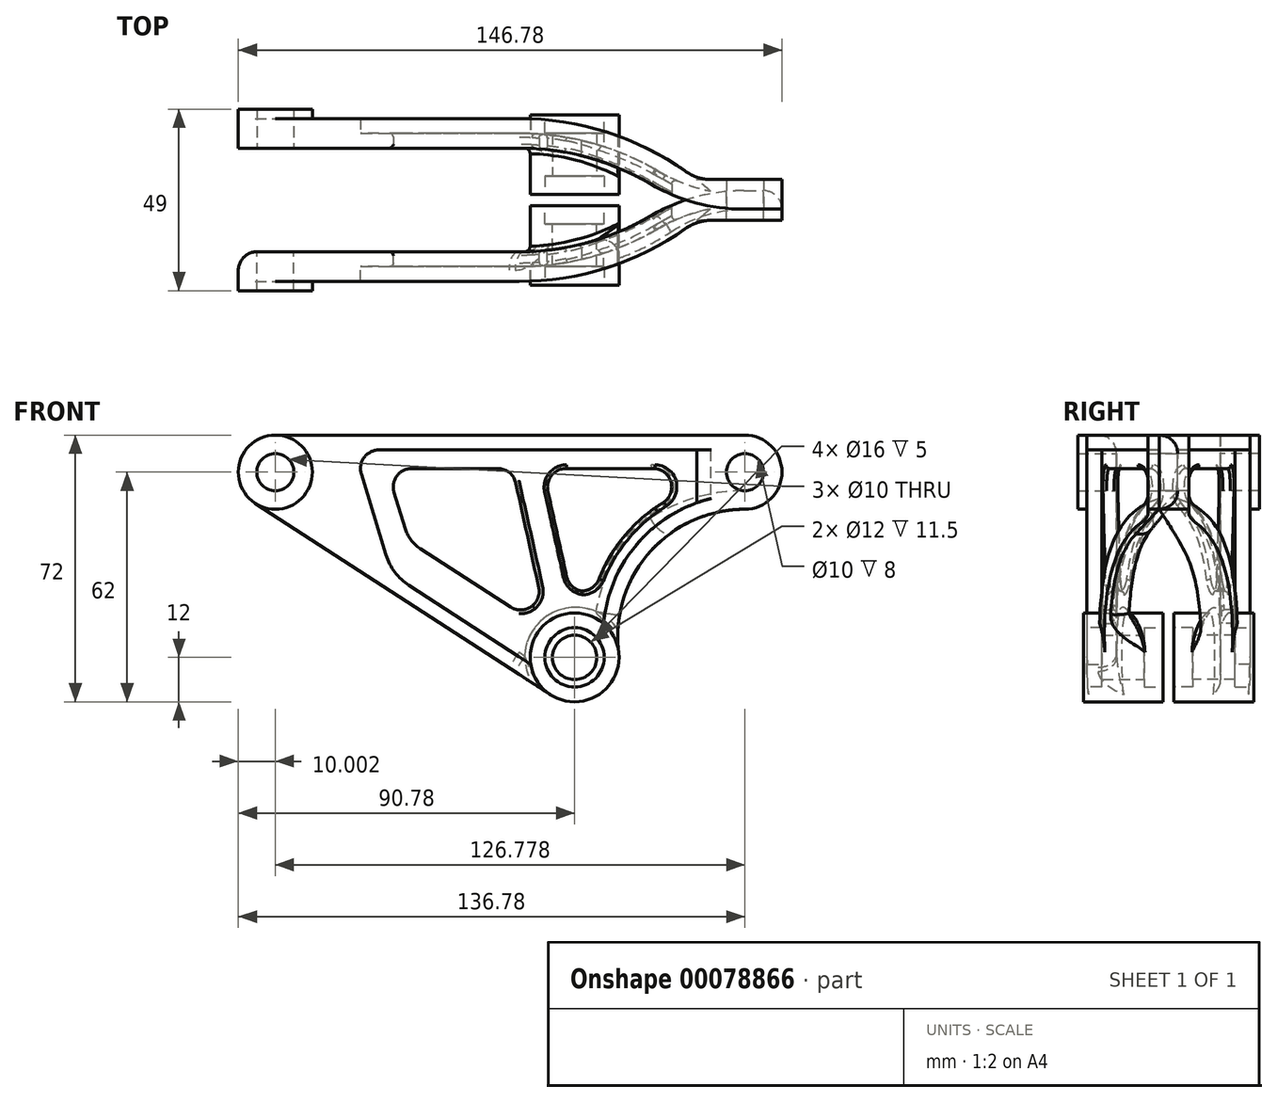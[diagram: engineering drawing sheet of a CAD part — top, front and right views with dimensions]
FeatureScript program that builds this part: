
annotation { "Feature Type Name" : "Feature", "Feature Type Description" : "" }
export const myFeature = defineFeature(function(context is Context, id is Id, definition is map)
    precondition{}
    {
        {
            var Q0;
            Q0=qCreatedBy(makeId("Front.planeOp"),FACE);
            var sketch = newSketch(context, id + "F0", { "sketchPlane" : qUnion([Q0])});
            skCircle(sketch, "E0", {"center": v(0, 0) * mm, "radius": 6 * mm});
            skCircle(sketch, "E1", {"center": v(0, 0) * mm, "radius": 12 * mm});
            skLineSegment(sketch, "E2", {"start": v(0, 0) * mm, "end": v(0, 50) * mm, "construction": true});
            skLineSegment(sketch, "E3", {"start": v(0, 50) * mm, "end": v(-80.78, 50) * mm, "construction": true});
            skLineSegment(sketch, "E4", {"start": v(-80.78, 50) * mm, "end": v(0, 0) * mm, "construction": true});
            skLineSegment(sketch, "E5", {"start": v(0, 0) * mm, "end": v(46, 50) * mm, "construction": true});
            skLineSegment(sketch, "E6", {"start": v(46, 50) * mm, "end": v(0, 50) * mm, "construction": true});
            skCircle(sketch, "E7", {"center": v(-80.78, 50) * mm, "radius": 10 * mm});
            skCircle(sketch, "E8", {"center": v(46, 50) * mm, "radius": 10 * mm});
            skCircle(sketch, "E9", {"center": v(46, 50) * mm, "radius": 6 * mm});
            skCircle(sketch, "E10", {"center": v(-80.78, 50) * mm, "radius": 6 * mm});
            skLineSegment(sketch, "E11", {"start": v(-80.78, 60) * mm, "end": v(46, 60) * mm});
            skLineSegment(sketch, "E12", {"start": v(-86.22, 41.6) * mm, "end": v(-6.53, -10.07) * mm});
            skLineSegment(sketch, "E13", {"start": v(53.56, 43.45) * mm, "end": v(9.07, -7.86) * mm, "construction": true});
            skArc(sketch, "E14", {"start": v(46, 40) * mm, "mid": v(20.27, 28.41) * mm, "end": v(11.91, 1.46) * mm});
            skSolve(sketch);
        }
        {
            var Q0;
            {var subQ0=makeQuery(id+"F0.imprint","IMPRINT",EDGE,{"derivedFrom":sQuery(id+"F0.wireOp",EDGE,"E0")});var subQ1=makeQuery(id+"F0.imprint","IMPRINT",EDGE,{"derivedFrom":sQuery(id+"F0.wireOp",EDGE,"E9")});var subQ2=makeQuery(id+"F0.imprint","IMPRINT",EDGE,{"derivedFrom":sQuery(id+"F0.wireOp",EDGE,"E10")});var subQ11=sQuery(id+"F0.wireOp",EDGE,"E11");Q0=qUnion([makeQuery(id+"F0.imprint","IMPRINT",FACE,{"disambiguationData":[TD([[subQ0,1.0]])]}),makeQuery(id+"F0.imprint","IMPRINT",FACE,{"disambiguationData":[TD([[subQ1,1.0]])]}),makeQuery(id+"F0.imprint","IMPRINT",FACE,{"disambiguationData":[TD([[subQ2,1.0]])]}),makeQuery(id+"F0.imprint","IMPRINT",FACE,{"disambiguationData":[TD([[subQ0,-1.0]])]}),makeQuery(id+"F0.imprint","IMPRINT",FACE,{"disambiguationData":[TD([[subQ2,-1.0]])]}),makeQuery(id+"F0.imprint","IMPRINT",FACE,{"disambiguationData":[TD([[subQ1,-1.0]])]}),makeQuery(id+"F0.imprint","IMPRINT",FACE,{"disambiguationData":[TD([[makeQuery(id+"F0.imprint","IMPRINT",EDGE,{"derivedFrom":subQ11}),-1.0]])]})]);}
            extrude(context, id + "F1", {"entities" : qUnion([Q0]), "depth" : 22 * mm});
        }
        {
            var Q0;
            Q0=makeQuery(id+"F1.opExtrude","CAP_FACE",FACE,{"disambiguationData":[OSD([sQuery(id+"F0.wireOp",EDGE,"E1"),sQuery(id+"F0.wireOp",EDGE,"E7"),sQuery(id+"F0.wireOp",EDGE,"E8"),sQuery(id+"F0.wireOp",EDGE,"E11"),sQuery(id+"F0.wireOp",EDGE,"E12"),sQuery(id+"F0.wireOp",EDGE,"E14")])],"isStart":true});
            extrude(context, id + "F2", {"entities" : qUnion([Q0]), "operationType" : NewBodyOperationType.ADD, "depth" : 2.5 * mm});
        }
        {
            var Q0;
            {var subQ0=sQuery(id+"F0.wireOp",EDGE,"E11");Q0=makeQuery(id+"F2.boolean.opBoolean","MERGE",FACE,{"derivedFrom":[makeQuery(id+"F1.opExtrude","SWEPT_FACE",FACE,{"disambiguationData":[OSD([subQ0])]}),makeQuery(id+"F2.opExtrude","SWEPT_FACE",FACE,{"disambiguationData":[OSD([subQ0])]})]});}
            var sketch = newSketch(context, id + "F3", { "sketchPlane" : qUnion([Q0])});
            skLineSegment(sketch, "E15", {"start": v(-100, -14) * mm, "end": v(-15, -14) * mm});
            skArc(sketch, "E16", {"start": v(-15, -14) * mm, "mid": v(15.45, -7.03) * mm, "end": v(39.84, 12.5) * mm});
            skLineSegment(sketch, "E17", {"start": v(-100, -14) * mm, "end": v(-100, 12.5) * mm});
            skLineSegment(sketch, "E18", {"start": v(-100, 12.5) * mm, "end": v(39.84, 12.5) * mm});
            skArc(sketch, "E19.0", {"start": v(-15, -22) * mm, "mid": v(10.37, -17.76) * mm, "end": v(32.98, -5.5) * mm});
            skLineSegment(sketch, "E20", {"start": v(-15, -22) * mm, "end": v(-15, -32) * mm});
            skLineSegment(sketch, "E21", {"start": v(-15, -32) * mm, "end": v(70, -32) * mm});
            skLineSegment(sketch, "E22", {"start": v(70, -32) * mm, "end": v(70, -5.5) * mm});
            skLineSegment(sketch, "E23", {"start": v(70, -5.5) * mm, "end": v(32.98, -5.5) * mm});
            skSolve(sketch);
        }
        {
            var Q0;
            {var subQ3=sQuery(id+"F3.wireOp",EDGE,"E15");var subQ8=sQuery(id+"F3.wireOp",EDGE,"E16");var subQ12=sQuery(id+"F3.wireOp",EDGE,"E17");var subQ20=sQuery(id+"F3.wireOp",EDGE,"E19.0");var subQ21=sQuery(id+"F3.wireOp",EDGE,"E20");var subQ24=makeQuery(id+"F3.imprint","INTERSECT",VERTEX,{"derivedFrom":[subQ3,subQ8]});Q0=qUnion([makeQuery(id+"F3.imprint","IMPRINT",FACE,{"disambiguationData":[TD([[makeQuery(id+"F3.imprint","IMPRINT",EDGE,{"derivedFrom":subQ12}),-1.0]])]}),makeQuery(id+"F3.imprint","IMPRINT",FACE,{"disambiguationData":[TD([[makeQuery(id+"F3.imprint","IMPRINT",EDGE,{"derivedFrom":subQ21}),1.0]])]}),makeQuery(id+"F3.imprint","IMPRINT",FACE,{"disambiguationData":[TD([[makeQuery(id+"F3.imprint","IMPRINT",EDGE,{"disambiguationData":[TD([[subQ24,-1.0]])],"derivedFrom":subQ8}),1.0]])]}),makeQuery(id+"F3.imprint","IMPRINT",FACE,{"disambiguationData":[TD([[makeQuery(id+"F3.imprint","IMPRINT",EDGE,{"derivedFrom":subQ20}),-1.0]])]})]);}
            extrude(context, id + "F4", {"entities" : qUnion([Q0]), "operationType" : NewBodyOperationType.REMOVE, "endBound" : BoundingType.THROUGH_ALL, "oppositeDirection" : true, "depth" : 25 * mm});
        }
        {
            var Q0;
            Q0=makeQuery(id+"F4.boolean.opBoolean","INTERSECT",EDGE,{"derivedFrom":[makeQuery(id+"F2.opExtrude","CAP_FACE",FACE,{"disambiguationData":[OSD([sQuery(id+"F0.wireOp",EDGE,"E1"),sQuery(id+"F0.wireOp",EDGE,"E7"),sQuery(id+"F0.wireOp",EDGE,"E8"),sQuery(id+"F0.wireOp",EDGE,"E11"),sQuery(id+"F0.wireOp",EDGE,"E12"),sQuery(id+"F0.wireOp",EDGE,"E14")])],"isStart":false}),makeQuery(id+"F4.opExtrude","SWEPT_FACE",FACE,{"disambiguationData":[OSD([sQuery(id+"F3.wireOp",EDGE,"E16")])]})]});
            var Q1;
            Q1=makeQuery(id+"F4.opExtrude","SWEPT_EDGE",EDGE,{"disambiguationData":[OSD([sQuery(id+"F3.imprint",VERTEX,"E19.0.end")])]});
            fillet(context, id + "F5", {"entities" : qUnion([Q0, Q1]), "radius" : 50 * mm, "tangentPropagation" : true, "allowEdgeOverflow" : false});
        }
        {
            var Q0;
            Q0=makeQuery(id+"F1.opExtrude","CAP_FACE",FACE,{"disambiguationData":[OSD([sQuery(id+"F0.wireOp",EDGE,"E1"),sQuery(id+"F0.wireOp",EDGE,"E7"),sQuery(id+"F0.wireOp",EDGE,"E8"),sQuery(id+"F0.wireOp",EDGE,"E11"),sQuery(id+"F0.wireOp",EDGE,"E12"),sQuery(id+"F0.wireOp",EDGE,"E14")])],"isStart":false});
            var Q1;
            Q1=makeQuery(id+"F4.opExtrude","SWEPT_FACE",FACE,{"disambiguationData":[OSD([sQuery(id+"F3.imprint",EDGE,"E19.0")])]});
            var Q2;
            Q2=makeQuery(id+"F5.opFillet","BLEND_FACE",FACE,{"disambiguationData":[OSD([sQuery(id+"F3.imprint",VERTEX,"E19.0.end")])]});
            var Q3;
            Q3=makeQuery(id+"F4.opExtrude","SWEPT_FACE",FACE,{"disambiguationData":[OSD([makeQuery(id+"F3.imprint","SKETCH_ENTITY",EDGE,{"disambiguationData":[TD([[sQuery(id+"F3.imprint",VERTEX,"E22.end"),-1.0]])],"sketchEntityId":"E23"})])]});
            var Q4;
            Q4=makeQuery(id+"F4.boolean.opBoolean","COPY",FACE,{"derivedFrom":makeQuery(id+"F4.opExtrude","SWEPT_FACE",FACE,{"disambiguationData":[OSD([sQuery(id+"F3.wireOp",EDGE,"E19.0")])]})});
            shell(context, id + "F6", {"entities" : qUnion([Q0, Q1, Q2, Q3, Q4]), "thickness" : 4 * mm});
        }
        {
            var Q0;
            Q0=makeQuery(id+"F0.imprint","IMPRINT",FACE,{"disambiguationData":[TD([[makeQuery(id+"F0.imprint","IMPRINT",EDGE,{"derivedFrom":sQuery(id+"F0.wireOp",EDGE,"E0")}),-1.0]])]});
            extrude(context, id + "F7", {"entities" : qUnion([Q0]), "operationType" : NewBodyOperationType.ADD, "depth" : 23 * mm});
        }
        {
            var Q0;
            Q0=makeQuery(id+"F1.opExtrude","CAP_FACE",FACE,{"disambiguationData":[OSD([sQuery(id+"F0.wireOp",EDGE,"E1"),sQuery(id+"F0.wireOp",EDGE,"E7"),sQuery(id+"F0.wireOp",EDGE,"E8"),sQuery(id+"F0.wireOp",EDGE,"E11"),sQuery(id+"F0.wireOp",EDGE,"E12"),sQuery(id+"F0.wireOp",EDGE,"E14")])],"isStart":false});
            var sketch = newSketch(context, id + "F8", { "sketchPlane" : qUnion([Q0])});
            skLineSegment(sketch, "E24", {"start": v(-60.78, 60) * mm, "end": v(-47.47, 16.48) * mm});
            skLineSegment(sketch, "E25.0", {"start": v(-80.78, 60) * mm, "end": v(-60.78, 60) * mm});
            skLineSegment(sketch, "E25.1", {"start": v(-86.22, 41.6) * mm, "end": v(-47.47, 16.48) * mm});
            skArc(sketch, "E26.trimmedOffspring", {"start": v(-80.78, 60) * mm, "mid": v(-90.37, 52.84) * mm, "end": v(-86.22, 41.6) * mm});
            skSolve(sketch);
        }
        {
            var Q0;
            {var subQ4=makeQuery(id+"F6.opShell","OFFSET_EDGE",EDGE,{"disambiguationData":[OSD([sQuery(id+"F0.wireOp",EDGE,"E7")])]});var subQ10=makeQuery(id+"F8.imprint","IMPRINT",EDGE,{"derivedFrom":subQ4});var subQ12=sQuery(id+"F8.wireOp",EDGE,"E25.0");Q0=qUnion([makeQuery(id+"F8.imprint","IMPRINT",FACE,{"disambiguationData":[TD([[subQ10,1.0]])]}),makeQuery(id+"F8.imprint","IMPRINT",FACE,{"disambiguationData":[TD([[makeQuery(id+"F8.imprint","IMPRINT",EDGE,{"derivedFrom":subQ12}),-1.0]])]})]);}
            extrude(context, id + "F9", {"entities" : qUnion([Q0]), "operationType" : NewBodyOperationType.ADD, "oppositeDirection" : true, "depth" : 6 * mm});
        }
        {
            var Q0;
            Q0=makeQuery(id+"F9.boolean.opBoolean","INTERSECT",EDGE,{"derivedFrom":[makeQuery(id+"F6.opShell","OFFSET_FACE",FACE,{"disambiguationData":[OSD([sQuery(id+"F0.wireOp",EDGE,"E12")])]}),makeQuery(id+"F9.opExtrude","SWEPT_FACE",FACE,{"disambiguationData":[OSD([sQuery(id+"F8.wireOp",EDGE,"E24")])]})]});
            fillet(context, id + "F10", {"entities" : qUnion([Q0]), "radius" : 15 * mm, "tangentPropagation" : true, "allowEdgeOverflow" : false});
        }
        {
            var Q0;
            Q0=makeQuery(id+"F9.boolean.opBoolean","INTERSECT",EDGE,{"derivedFrom":[makeQuery(id+"F6.opShell","OFFSET_FACE",FACE,{"disambiguationData":[OSD([sQuery(id+"F0.wireOp",EDGE,"E11")])]}),makeQuery(id+"F9.opExtrude","SWEPT_FACE",FACE,{"disambiguationData":[OSD([sQuery(id+"F8.wireOp",EDGE,"E24")])]})]});
            fillet(context, id + "F11", {"entities" : qUnion([Q0]), "radius" : 5 * mm, "tangentPropagation" : true, "allowEdgeOverflow" : false});
        }
        {
            var Q0;
            Q0=makeQuery(id+"F4.boolean.opBoolean","COPY",FACE,{"derivedFrom":makeQuery(id+"F4.opExtrude","SWEPT_FACE",FACE,{"disambiguationData":[OSD([sQuery(id+"F3.wireOp",EDGE,"E23")])]})});
            var sketch = newSketch(context, id + "F12", { "sketchPlane" : qUnion([Q0])});
            skCircle(sketch, "E27", {"center": v(46, 50) * mm, "radius": 10 * mm});
            skSolve(sketch);
        }
        {
            var Q0;
            Q0=makeQuery(id+"F9.boolean.opBoolean","MERGE",FACE,{"derivedFrom":[makeQuery(id+"F1.opExtrude","CAP_FACE",FACE,{"disambiguationData":[OSD([sQuery(id+"F0.wireOp",EDGE,"E1"),sQuery(id+"F0.wireOp",EDGE,"E7"),sQuery(id+"F0.wireOp",EDGE,"E8"),sQuery(id+"F0.wireOp",EDGE,"E11"),sQuery(id+"F0.wireOp",EDGE,"E12"),sQuery(id+"F0.wireOp",EDGE,"E14")])],"isStart":false}),makeQuery(id+"F9.opExtrude","CAP_FACE",FACE,{"disambiguationData":[OSD([sQuery(id+"F8.wireOp",EDGE,"E24"),sQuery(id+"F8.wireOp",EDGE,"E25.0"),sQuery(id+"F8.wireOp",EDGE,"E25.1"),sQuery(id+"F8.wireOp",EDGE,"E26.trimmedOffspring")])],"isStart":true})]});
            var sketch = newSketch(context, id + "F13", { "sketchPlane" : qUnion([Q0])});
            skCircle(sketch, "E28", {"center": v(-80.78, 50) * mm, "radius": 10 * mm});
            skSolve(sketch);
        }
        {
            var Q0;
            {var subQ0=sQuery(id+"F13.wireOp",EDGE,"E28");var subQ2=makeQuery(id+"F13.imprint","INTERSECT",VERTEX,{"derivedFrom":[makeQuery(id+"F1.opExtrude","CAP_EDGE",EDGE,{"disambiguationData":[OSD([sQuery(id+"F0.wireOp",EDGE,"E11")])],"isStart":false}),subQ0]});Q0=makeQuery(id+"F13.imprint","IMPRINT",FACE,{"disambiguationData":[TD([[makeQuery(id+"F13.imprint","IMPRINT",EDGE,{"disambiguationData":[TD([[subQ2,-1.0]])],"derivedFrom":subQ0}),1.0]])]});}
            extrude(context, id + "F14", {"entities" : qUnion([Q0]), "operationType" : NewBodyOperationType.ADD, "depth" : 2.5 * mm});
        }
        {
            var Q0;
            Q0=qCreatedBy(makeId("Front.planeOp"),FACE);
            var sketch = newSketch(context, id + "F15", { "sketchPlane" : qUnion([Q0])});
            skLineSegment(sketch, "E29", {"start": v(-43.95, 51) * mm, "end": v(-16.73, 51) * mm});
            skLineSegment(sketch, "E30", {"start": v(-48.73, 44.54) * mm, "end": v(-45.77, 34.86) * mm});
            skLineSegment(sketch, "E31", {"start": v(-41.65, 29.4) * mm, "end": v(-13.92, 11.41) * mm});
            skLineSegment(sketch, "E32", {"start": v(-16.73, 51) * mm, "end": v(-8.96, 15.61) * mm});
            skPoint(sketch, "E33.visualSharp", {"position": v(-50.7, 51) * mm});
            skArc(sketch, "E33.filletArc", {"start": v(-43.95, 51) * mm, "mid": v(-47.97, 48.97) * mm, "end": v(-48.73, 44.54) * mm});
            skPoint(sketch, "E34.visualSharp", {"position": v(-44.7, 31.38) * mm});
            skArc(sketch, "E34.filletArc", {"start": v(-45.77, 34.86) * mm, "mid": v(-44.2, 31.76) * mm, "end": v(-41.65, 29.4) * mm});
            skArc(sketch, "E35.trimOffspring", {"start": v(-8.96, 15.61) * mm, "mid": v(-11.63, 13.74) * mm, "end": v(-13.92, 11.41) * mm});
            skLineSegment(sketch, "E36", {"start": v(-8.54, 51) * mm, "end": v(21.22, 51) * mm});
            skLineSegment(sketch, "E37", {"start": v(-8.54, 51) * mm, "end": v(-1.28, 17.95) * mm});
            skArc(sketch, "E38", {"start": v(5.26, 17.21) * mm, "mid": v(2.03, 17.89) * mm, "end": v(-1.28, 17.95) * mm});
            skArc(sketch, "E39", {"start": v(23.84, 41.74) * mm, "mid": v(12.25, 31.22) * mm, "end": v(5.26, 17.21) * mm});
            skArc(sketch, "E40", {"start": v(21.22, 51) * mm, "mid": v(26.04, 47.36) * mm, "end": v(23.84, 41.74) * mm});
            skLineSegment(sketch, "E41", {"start": v(0, 0) * mm, "end": v(-19.78, 90.06) * mm, "construction": true});
            skSolve(sketch);
        }
        {
            var Q0;
            {Q0=qUnion([makeQuery(id+"F15.imprint","IMPRINT",FACE,{"disambiguationData":[TD([[makeQuery(id+"F15.imprint","IMPRINT",EDGE,{"derivedFrom":sQuery(id+"F15.wireOp",EDGE,"E29")}),-1.0]])]}),makeQuery(id+"F15.imprint","IMPRINT",FACE,{"disambiguationData":[TD([[makeQuery(id+"F15.imprint","IMPRINT",EDGE,{"derivedFrom":sQuery(id+"F15.wireOp",EDGE,"E36")}),-1.0]])]})]);}
            extrude(context, id + "F16", {"entities" : qUnion([Q0]), "operationType" : NewBodyOperationType.REMOVE, "endBound" : BoundingType.SYMMETRIC, "depth" : 50 * mm});
        }
        {
            var Q0;
            Q0=makeQuery(id+"F6.opShell","OFFSET_EDGE",EDGE,{"disambiguationData":[OSD([sQuery(id+"F3.wireOp",EDGE,"E19.0"),sQuery(id+"F3.wireOp",EDGE,"E23")]),OD(0.0)]});
            var Q1;
            Q1=makeQuery(id+"F4.boolean.opBoolean","COPY",EDGE,{"derivedFrom":makeQuery(id+"F4.opExtrude","SWEPT_EDGE",EDGE,{"disambiguationData":[OSD([sQuery(id+"F3.wireOp",EDGE,"E19.0"),sQuery(id+"F3.wireOp",EDGE,"E23")])]})});
            fillet(context, id + "F17", {"entities" : qUnion([Q0, Q1]), "radius" : 12 * mm, "tangentPropagation" : true, "allowEdgeOverflow" : false});
        }
        {
            var Q0;
            Q0=makeQuery(id+"F16.boolean.opBoolean","COPY",EDGE,{"derivedFrom":makeQuery(id+"F16.opExtrude","SWEPT_EDGE",EDGE,{"disambiguationData":[OSD([sQuery(id+"F15.wireOp",EDGE,"E29"),sQuery(id+"F15.wireOp",EDGE,"E32")])]})});
            var Q1;
            Q1=makeQuery(id+"F16.boolean.opBoolean","COPY",EDGE,{"derivedFrom":makeQuery(id+"F16.opExtrude","SWEPT_EDGE",EDGE,{"disambiguationData":[OSD([sQuery(id+"F15.wireOp",EDGE,"E31"),sQuery(id+"F15.wireOp",EDGE,"E35.trimOffspring")])]})});
            var Q2;
            Q2=makeQuery(id+"F16.boolean.opBoolean","COPY",EDGE,{"derivedFrom":makeQuery(id+"F16.opExtrude","SWEPT_EDGE",EDGE,{"disambiguationData":[OSD([sQuery(id+"F15.wireOp",EDGE,"E38"),sQuery(id+"F15.wireOp",EDGE,"E39")])]})});
            var Q3;
            Q3=makeQuery(id+"F16.boolean.opBoolean","COPY",EDGE,{"derivedFrom":makeQuery(id+"F16.opExtrude","SWEPT_EDGE",EDGE,{"disambiguationData":[OSD([sQuery(id+"F15.wireOp",EDGE,"E37"),sQuery(id+"F15.wireOp",EDGE,"E38")])]})});
            var Q4;
            Q4=makeQuery(id+"F16.boolean.opBoolean","COPY",EDGE,{"derivedFrom":makeQuery(id+"F16.opExtrude","SWEPT_EDGE",EDGE,{"disambiguationData":[OSD([sQuery(id+"F15.wireOp",EDGE,"E32"),sQuery(id+"F15.wireOp",EDGE,"E35.trimOffspring")])]})});
            var Q5;
            Q5=makeQuery(id+"F16.boolean.opBoolean","COPY",EDGE,{"derivedFrom":makeQuery(id+"F16.opExtrude","SWEPT_EDGE",EDGE,{"disambiguationData":[OSD([sQuery(id+"F15.wireOp",EDGE,"E36"),sQuery(id+"F15.wireOp",EDGE,"E37")])]})});
            fillet(context, id + "F18", {"entities" : qUnion([Q0, Q1, Q2, Q3, Q4, Q5]), "radius" : 5 * mm, "tangentPropagation" : true, "allowEdgeOverflow" : false});
        }
        {
            var Q0;
            {var subQ0=sQuery(id+"F3.wireOp",EDGE,"E16");var subQ1=sQuery(id+"F0.wireOp",EDGE,"E1");Q0=makeQuery(id+"F16.boolean.opBoolean","INTERSECT",EDGE,{"derivedFrom":[makeQuery(id+"F7.boolean.opBoolean","SPLIT",FACE,{"disambiguationData":[TD([makeQuery(id+"F1.opExtrude","SWEPT_FACE",FACE,{"disambiguationData":[OSD([subQ1])]})])],"derivedFrom":makeQuery(id+"F6.opShell","OFFSET_FACE",FACE,{"disambiguationData":[OSD([subQ0])]})}),makeQuery(id+"F16.opExtrude","SWEPT_FACE",FACE,{"disambiguationData":[OSD([sQuery(id+"F15.wireOp",EDGE,"E36")])]})]});}
            var Q1;
            Q1=makeQuery(id+"F16.boolean.opBoolean","INTERSECT",EDGE,{"derivedFrom":[makeQuery(id+"F6.opShell","OFFSET_FACE",FACE,{"disambiguationData":[OSD([sQuery(id+"F3.wireOp",EDGE,"E15")])]}),makeQuery(id+"F16.opExtrude","SWEPT_FACE",FACE,{"disambiguationData":[OSD([sQuery(id+"F15.wireOp",EDGE,"E29")])]})]});
            var Q2;
            Q2=makeQuery(id+"F16.boolean.opBoolean","INTERSECT",EDGE,{"derivedFrom":[makeQuery(id+"F5.opFillet","BLEND_FACE",FACE,{"disambiguationData":[OSD([sQuery(id+"F0.wireOp",EDGE,"E1"),sQuery(id+"F0.wireOp",EDGE,"E7"),sQuery(id+"F0.wireOp",EDGE,"E8"),sQuery(id+"F0.wireOp",EDGE,"E11"),sQuery(id+"F0.wireOp",EDGE,"E12"),sQuery(id+"F0.wireOp",EDGE,"E14"),sQuery(id+"F3.wireOp",EDGE,"E16")])]}),makeQuery(id+"F16.opExtrude","SWEPT_FACE",FACE,{"disambiguationData":[OSD([sQuery(id+"F15.wireOp",EDGE,"E40")])]})]});
            var Q3;
            {var subQ0=sQuery(id+"F3.wireOp",EDGE,"E16");var subQ1=sQuery(id+"F0.wireOp",EDGE,"E1");Q3=makeQuery(id+"F16.boolean.opBoolean","INTERSECT",EDGE,{"derivedFrom":[makeQuery(id+"F7.boolean.opBoolean","SPLIT",FACE,{"disambiguationData":[TD([makeQuery(id+"F1.opExtrude","SWEPT_FACE",FACE,{"disambiguationData":[OSD([subQ1])]})])],"derivedFrom":makeQuery(id+"F4.boolean.opBoolean","COPY",FACE,{"derivedFrom":makeQuery(id+"F4.opExtrude","SWEPT_FACE",FACE,{"disambiguationData":[OSD([subQ0])]})})}),makeQuery(id+"F16.opExtrude","SWEPT_FACE",FACE,{"disambiguationData":[OSD([sQuery(id+"F15.wireOp",EDGE,"E32")])]})]});}
            fillet(context, id + "F19", {"entities" : qUnion([Q0, Q1, Q2, Q3]), "radius" : 1 * mm, "tangentPropagation" : true, "allowEdgeOverflow" : false});
        }
        {
            var Q0;
            Q0=qCreatedBy(makeId("Front.planeOp"),FACE);
            var sketch = newSketch(context, id + "F20", { "sketchPlane" : qUnion([Q0])});
            skCircle(sketch, "E42", {"center": v(0, 0) * mm, "radius": 6 * mm});
            skCircle(sketch, "E43", {"center": v(46, 50) * mm, "radius": 5 * mm});
            skCircle(sketch, "E44", {"center": v(-80.78, 50) * mm, "radius": 5 * mm});
            skSolve(sketch);
        }
        {
            var Q0;
            {Q0=qUnion([makeQuery(id+"F20.imprint","IMPRINT",FACE,{"disambiguationData":[TD([[makeQuery(id+"F20.imprint","IMPRINT",EDGE,{"derivedFrom":sQuery(id+"F20.wireOp",EDGE,"E42")}),1.0]])]}),makeQuery(id+"F20.imprint","IMPRINT",FACE,{"disambiguationData":[TD([[makeQuery(id+"F20.imprint","IMPRINT",EDGE,{"derivedFrom":sQuery(id+"F20.wireOp",EDGE,"E43")}),1.0]])]}),makeQuery(id+"F20.imprint","IMPRINT",FACE,{"disambiguationData":[TD([[makeQuery(id+"F20.imprint","IMPRINT",EDGE,{"derivedFrom":sQuery(id+"F20.wireOp",EDGE,"E44")}),1.0]])]})]);}
            extrude(context, id + "F21", {"entities" : qUnion([Q0]), "operationType" : NewBodyOperationType.REMOVE, "endBound" : BoundingType.SYMMETRIC, "depth" : 50 * mm});
        }
        {
            var Q0;
            Q0=makeQuery(id+"F7.opExtrude","CAP_FACE",FACE,{"disambiguationData":[OSD([sQuery(id+"F0.wireOp",EDGE,"E0"),sQuery(id+"F0.wireOp",EDGE,"E1")])],"isStart":true});
            extrude(context, id + "F22", {"entities" : qUnion([Q0]), "operationType" : NewBodyOperationType.REMOVE, "oppositeDirection" : true, "depth" : 1.5 * mm});
        }
        {
            var Q0;
            Q0=makeQuery(id+"F7.opExtrude","CAP_FACE",FACE,{"disambiguationData":[OSD([sQuery(id+"F0.wireOp",EDGE,"E0"),sQuery(id+"F0.wireOp",EDGE,"E1")])],"isStart":false});
            var sketch = newSketch(context, id + "F23", { "sketchPlane" : qUnion([Q0])});
            skCircle(sketch, "E45", {"center": v(0, 0) * mm, "radius": 8 * mm});
            skSolve(sketch);
        }
        {
            var Q0;
            {var subQ0=makeQuery(id+"F23.imprint","IMPRINT",EDGE,{"derivedFrom":makeQuery(id+"F7.opExtrude","CAP_EDGE",EDGE,{"disambiguationData":[OSD([sQuery(id+"F0.wireOp",EDGE,"E0")])],"isStart":false})});Q0=qUnion([makeQuery(id+"F23.imprint","IMPRINT",FACE,{"disambiguationData":[TD([[subQ0,1.0]])]}),makeQuery(id+"F23.imprint","IMPRINT",FACE,{"disambiguationData":[TD([[makeQuery(id+"F23.imprint","IMPRINT",EDGE,{"derivedFrom":sQuery(id+"F23.wireOp",EDGE,"E45")}),1.0]])]})]);}
            extrude(context, id + "F24", {"entities" : qUnion([Q0]), "operationType" : NewBodyOperationType.REMOVE, "oppositeDirection" : true, "depth" : 5 * mm});
        }
        {
            var Q0;
            Q0=makeQuery(id+"F22.boolean.opBoolean","COPY",FACE,{"derivedFrom":makeQuery(id+"F22.opExtrude","CAP_FACE",FACE,{"disambiguationData":[OSD([sQuery(id+"F0.wireOp",EDGE,"E0"),sQuery(id+"F0.wireOp",EDGE,"E1")])],"isStart":false})});
            var sketch = newSketch(context, id + "F25", { "sketchPlane" : qUnion([Q0])});
            skCircle(sketch, "E46", {"center": v(0, 0) * mm, "radius": 8 * mm});
            skSolve(sketch);
        }
        {
            var Q0;
            {var subQ0=makeQuery(id+"F25.imprint","IMPRINT",EDGE,{"derivedFrom":makeQuery(id+"F22.boolean.opBoolean","COPY",EDGE,{"derivedFrom":makeQuery(id+"F22.opExtrude","CAP_EDGE",EDGE,{"disambiguationData":[OSD([sQuery(id+"F0.wireOp",EDGE,"E0")])],"isStart":false})})});Q0=qUnion([makeQuery(id+"F25.imprint","IMPRINT",FACE,{"disambiguationData":[TD([[subQ0,-1.0]])]}),makeQuery(id+"F25.imprint","IMPRINT",FACE,{"disambiguationData":[TD([[makeQuery(id+"F25.imprint","IMPRINT",EDGE,{"derivedFrom":sQuery(id+"F25.wireOp",EDGE,"E46")}),1.0]])]})]);}
            extrude(context, id + "F26", {"entities" : qUnion([Q0]), "operationType" : NewBodyOperationType.REMOVE, "oppositeDirection" : true, "depth" : 5 * mm});
        }
        {
            var Q0;
            Q0=makeQuery(id+"F7.boolean.opBoolean","INTERSECT",EDGE,{"derivedFrom":[makeQuery(id+"F4.boolean.opBoolean","COPY",FACE,{"derivedFrom":makeQuery(id+"F4.opExtrude","SWEPT_FACE",FACE,{"disambiguationData":[OSD([sQuery(id+"F3.wireOp",EDGE,"E16")])]})}),makeQuery(id+"F7.opExtrude","SWEPT_FACE",FACE,{"disambiguationData":[OSD([sQuery(id+"F0.wireOp",EDGE,"E1")])]})]});
            fillet(context, id + "F27", {"entities" : qUnion([Q0]), "radius" : 1.5 * mm, "tangentPropagation" : true, "allowEdgeOverflow" : false});
        }
        {
            var Q0;
            Q0=makeQuery(id+"F1.opExtrude","SWEPT_BODY",BODY,{"disambiguationData":[OSD([sQuery(id+"F0.wireOp",EDGE,"E1"),sQuery(id+"F0.wireOp",EDGE,"E7"),sQuery(id+"F0.wireOp",EDGE,"E8"),sQuery(id+"F0.wireOp",EDGE,"E11"),sQuery(id+"F0.wireOp",EDGE,"E12"),sQuery(id+"F0.wireOp",EDGE,"E14")])]});
            var Q1;
            Q1=qCreatedBy(makeId("Front.planeOp"),FACE);
            mirror(context, id + "F28", {"entities" : qUnion([Q0]), "mirrorPlane" : qUnion([Q1])});
        }
        {
            var Q0;
            Q0=makeQuery(id+"F4.boolean.opBoolean","COPY",EDGE,{"derivedFrom":makeQuery(id+"F4.opExtrude","CAP_EDGE",EDGE,{"disambiguationData":[OSD([sQuery(id+"F3.wireOp",EDGE,"E15")])],"isStart":true})});
            var Q1;
            {var subQ0=sQuery(id+"F0.wireOp",EDGE,"E7");Q1=makeQuery(id+"F4.boolean.opBoolean","INTERSECT",EDGE,{"derivedFrom":[makeQuery(id+"F2.boolean.opBoolean","MERGE",FACE,{"derivedFrom":[makeQuery(id+"F1.opExtrude","SWEPT_FACE",FACE,{"disambiguationData":[OSD([subQ0])]}),makeQuery(id+"F2.opExtrude","SWEPT_FACE",FACE,{"disambiguationData":[OSD([subQ0])]})]}),makeQuery(id+"F4.opExtrude","SWEPT_FACE",FACE,{"disambiguationData":[OSD([sQuery(id+"F3.wireOp",EDGE,"E15")])]})]});}
            var Q2;
            {var subQ0=sQuery(id+"F0.wireOp",EDGE,"E12");Q2=makeQuery(id+"F4.boolean.opBoolean","INTERSECT",EDGE,{"derivedFrom":[makeQuery(id+"F2.boolean.opBoolean","MERGE",FACE,{"derivedFrom":[makeQuery(id+"F1.opExtrude","SWEPT_FACE",FACE,{"disambiguationData":[OSD([subQ0])]}),makeQuery(id+"F2.opExtrude","SWEPT_FACE",FACE,{"disambiguationData":[OSD([subQ0])]})]}),makeQuery(id+"F4.opExtrude","SWEPT_FACE",FACE,{"disambiguationData":[OSD([sQuery(id+"F3.wireOp",EDGE,"E15")])]})]});}
            fillet(context, id + "F29", {"entities" : qUnion([Q0, Q1, Q2]), "radius" : 5 * mm, "tangentPropagation" : true, "allowEdgeOverflow" : false});
        }
    });
